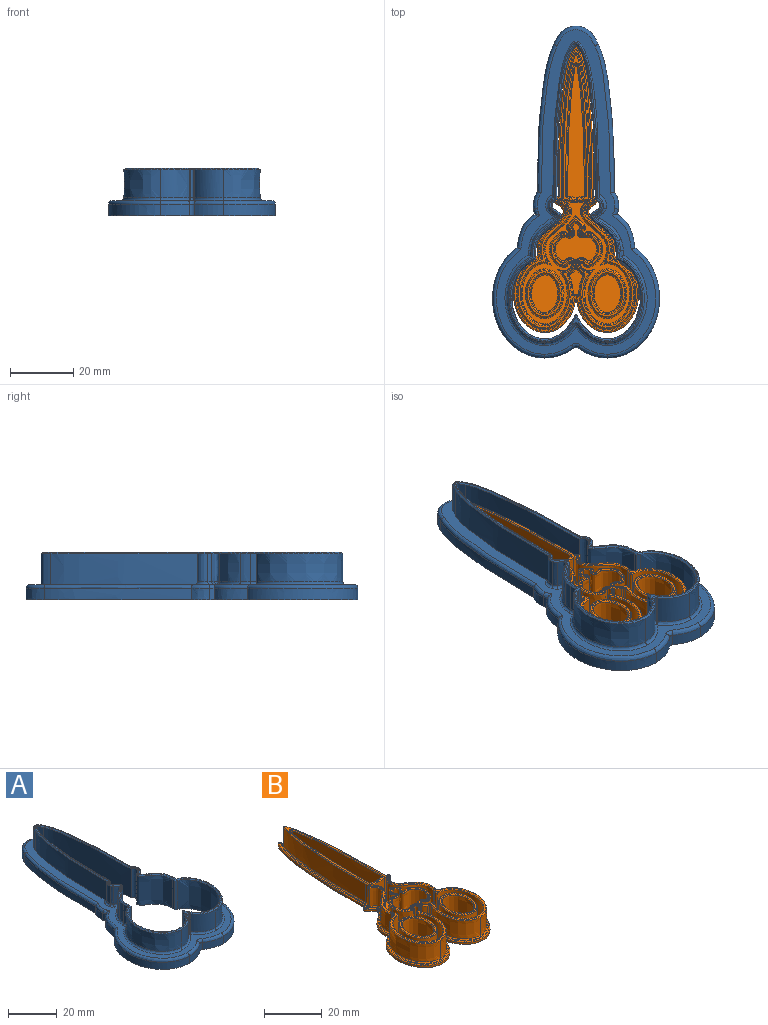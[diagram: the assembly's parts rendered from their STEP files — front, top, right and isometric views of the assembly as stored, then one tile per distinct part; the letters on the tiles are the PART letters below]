
ASSEMBLY  parts=2 mates=1
PART A: 138 faces, bbox 125.3x309.9x15.5 mm
  f0: extruded ~27.05x11.63mm, area 320.1mm2, adj f1,f15,f88,f136
  f1: extruded ~8.88x2.07mm, area 18.4mm2, adj f0,f2,f86,f137
  f2: extruded ~8.88x3.15mm, area 28.7mm2, adj f1,f3,f84,f135
  f3: extruded ~8.88x6.52mm, area 83.1mm2, adj f2,f16,f82,f133
  f4: extruded ~8.88x1.19mm, area 13.1mm2, adj f5,f16,f74,f129
  f5: extruded ~8.88x3.27mm, area 33.3mm2, adj f4,f6,f72,f127
  f6: extruded ~46.18x9.78mm, area 455.9mm2, adj f5,f7,f57,f72,f125
  f7: extruded ~9.78x5.38mm, area 83.8mm2, adj f6,f8,f57,f123
  f8: extruded ~46.22x9.78mm, area 456mm2, adj f7,f9,f57,f73,f121
  f9: extruded ~8.88x3.28mm, area 33.6mm2, adj f8,f10,f73,f119
  f10: extruded ~8.88x1.12mm, area 12.3mm2, adj f9,f17,f75,f117
  f11: extruded ~8.88x6.52mm, area 83.1mm2, adj f12,f17,f83,f114
  f12: extruded ~8.88x3.17mm, area 28.9mm2, adj f11,f18,f85,f116
  f13: extruded ~27.03x11.63mm, area 319.7mm2, adj f14,f18,f89,f120
  f14: extruded ~9.08x8.88mm, area 96.8mm2, adj f13,f19,f91,f122
  f15: extruded ~9.08x8.88mm, area 96.8mm2, adj f0,f22,f90,f134
  f16: extruded ~8.88x2.56mm, area 33mm2, adj f3,f4,f76,f78,f80,f131
  f17: extruded ~8.88x2.59mm, area 33.3mm2, adj f10,f11,f77,f79,f81,f115
  f18: extruded ~8.88x2.06mm, area 18.3mm2, adj f12,f13,f87,f118
  f19: extruded ~8.88x0.05mm, area 0.5mm2, adj f14,f20,f93,f124
  f20: extruded ~8.88x0.23mm, area 2.4mm2, adj f19,f95,f96,f126
  f21: extruded ~8.88x0.23mm, area 2.4mm2, adj f22,f94,f96,f130
  f22: extruded ~8.88x0.05mm, area 0.5mm2, adj f15,f21,f92,f132
  f23: extruded ~15.18x14.58mm, area 287.7mm2, adj f24,f40,f42,f102
  f24: extruded ~14.58x1.23mm, area 17.9mm2, adj f23,f25,f42,f103
  f25: extruded ~14.58x1.25mm, area 19.9mm2, adj f24,f26,f42,f104
  f26: extruded ~24.58x14.58mm, area 472.3mm2, adj f25,f27,f42,f105
  f27: extruded ~14.58x9.26mm, area 178mm2, adj f26,f28,f42,f106
  f28: extruded ~14.58x0.14mm, area 2.2mm2, adj f27,f29,f42,f106
  f29: extruded ~14.88x1.1mm, area 23.8mm2, adj f28,f30,f42,f106,f107
  f30: extruded ~14.58x0.14mm, area 2.2mm2, adj f29,f31,f42,f107
  f31: extruded ~14.58x9.26mm, area 178mm2, adj f30,f32,f42,f109
  f32: extruded ~24.58x14.58mm, area 472mm2, adj f31,f33,f42,f111
  f33: extruded ~14.58x1.25mm, area 19.7mm2, adj f32,f34,f42,f112
  f34: extruded ~14.58x1.22mm, area 17.9mm2, adj f33,f35,f42,f110
  f35: extruded ~15.1x14.58mm, area 286.2mm2, adj f34,f36,f42,f108
  f36: extruded ~14.76x2.94mm, area 45.4mm2, adj f35,f37,f42,f98,f108,f113
  f37: extruded ~46.33x14.58mm, area 681.9mm2, adj f36,f38,f42,f98
  f38: extruded ~14.58x3.23mm, area 86.1mm2, adj f37,f39,f42,f99
  f39: extruded ~46.32x14.58mm, area 682.2mm2, adj f38,f40,f42,f100
  f40: extruded ~14.58x2.36mm, area 43.4mm2, adj f23,f39,f42,f101
  f41: plane 94.61x42.81mm, normal (0,0,1), area 97.1mm2, adj f98,f99,f100,f101,f102,f103,f104,f105
  f42: plane 104.58x52.6mm, normal (0,0,-1), area 1523.6mm2, adj f23,f24,f25,f26,f27,f28,f29,f30
  f43: extruded ~10.54x5.63mm, area 44.7mm2, adj f42,f44,f56,f66
  f44: extruded ~34.78x16.43mm, area 166.3mm2, adj f42,f43,f45,f64
  f45: extruded ~9.14x3.6mm, area 35.4mm2, adj f42,f44,f46,f62
  f46: cylinder r=1.2mm len=3.6mm, axis (0,0,-1), area 5.6mm2, adj f42,f45,f47,f60
  f47: extruded ~9.14x3.6mm, area 35.4mm2, adj f42,f46,f48,f58
  f48: extruded ~34.78x16.43mm, area 166.3mm2, adj f42,f47,f49,f59
  f49: extruded ~10.53x5.63mm, area 44.7mm2, adj f42,f48,f50,f61
  f50: extruded ~3.6x1.55mm, area 5.9mm2, adj f42,f49,f51,f63,f65
  f51: extruded ~5.54x3.6mm, area 20.9mm2, adj f42,f50,f52,f65
  f52: extruded ~46.44x5.18mm, area 169.2mm2, adj f42,f51,f53,f67
  f53: extruded ~13.99x5.73mm, area 69.1mm2, adj f42,f52,f54,f69
  f54: extruded ~46.55x5.1mm, area 169.5mm2, adj f42,f53,f55,f71
  f55: extruded ~5.44x3.6mm, area 20.6mm2, adj f42,f54,f56,f70
  f56: extruded ~3.6x1.55mm, area 5.8mm2, adj f42,f43,f55,f68
  f57: plane 102.19x50.2mm, normal (0,0,1), area 781.1mm2, adj f6,f7,f8,f58,f59,f60,f61,f62
  f58: bspline ~11.07x5.19mm, area 18mm2, adj f47,f57,f59,f60
  f59: bspline ~35.48x27.64mm, area 85.5mm2, adj f48,f57,f58,f61
  f60: torus R=2.4mm, axis (0,0,-1), area 4mm2, adj f46,f57,f58,f62
  f61: bspline ~16.17x12.72mm, area 24.2mm2, adj f49,f57,f59,f63
  f62: bspline ~11.07x5.19mm, area 18mm2, adj f45,f57,f60,f64
  f63: bspline ~3.23x2.2mm, area 3.8mm2, adj f50,f57,f61,f65
  f64: bspline ~35.48x27.64mm, area 85.5mm2, adj f44,f57,f62,f66
  f65: bspline ~7.84x3.36mm, area 10.6mm2, adj f50,f51,f57,f63,f67
  f66: bspline ~17.19x13.49mm, area 24.2mm2, adj f43,f57,f64,f68
  f67: bspline ~64.82x9.6mm, area 88.6mm2, adj f52,f57,f65,f69
  f68: bspline ~3.55x2.44mm, area 3.8mm2, adj f56,f57,f66,f70
  f69: bspline ~20.23x12.76mm, area 34.5mm2, adj f53,f57,f67,f71
  f70: bspline ~6.73x2.7mm, area 10.6mm2, adj f55,f57,f68,f71
  f71: bspline ~261.75x110.62mm, area 88.8mm2, adj f54,f57,f69,f70
  f72: bspline ~4.93x3mm, area 6.3mm2, adj f5,f6,f57,f74
  f73: bspline ~5.31x3.48mm, area 6.4mm2, adj f8,f9,f57,f75
  f74: bspline ~2.52x2.18mm, area 2.4mm2, adj f4,f57,f72,f76
  f75: bspline ~2.24x2.03mm, area 2.2mm2, adj f10,f57,f73,f77
  f76: bspline ~2.36x1.96mm, area 2.2mm2, adj f16,f57,f74,f78
  f77: bspline ~2.38x1.96mm, area 2.3mm2, adj f17,f57,f75,f79
  f78: bspline ~1.09x1.03mm, area 0.7mm2, adj f16,f76,f80
  f79: bspline ~1.09x1.03mm, area 0.7mm2, adj f17,f77,f81
  f80: bspline ~1.39x1.32mm, area 0.9mm2, adj f16,f57,f78,f82
  f81: bspline ~1.41x1.32mm, area 0.9mm2, adj f17,f57,f79,f83
  f82: bspline ~11.13x10.28mm, area 13.5mm2, adj f3,f57,f80,f84
  f83: bspline ~11.04x10.19mm, area 13.5mm2, adj f11,f57,f81,f85
  f84: bspline ~4.22x1.67mm, area 4.7mm2, adj f2,f57,f82,f86
  f85: bspline ~4.66x1.85mm, area 4.7mm2, adj f12,f57,f83,f87
  f86: bspline ~3.08x0.98mm, area 2.6mm2, adj f1,f57,f84,f88
  f87: bspline ~3.17x1.01mm, area 2.6mm2, adj f18,f57,f85,f89
  f88: bspline ~28.88x24.5mm, area 51.8mm2, adj f0,f57,f86,f90
  f89: bspline ~28.88x24.5mm, area 51.7mm2, adj f13,f57,f87,f91
  f90: bspline ~10.44x6.32mm, area 15.9mm2, adj f15,f57,f88,f92
  f91: bspline ~10.44x6.32mm, area 15.9mm2, adj f14,f57,f89,f93
  f92: bspline ~0.9x0.79mm, area 0.1mm2, adj f22,f57,f90,f94
  f93: bspline ~0.9x0.79mm, area 0.1mm2, adj f19,f57,f91,f95
  f94: bspline ~1.75x1.59mm, area 0.3mm2, adj f21,f57,f92,f97
  f95: bspline ~1.17x1.12mm, area 0.3mm2, adj f20,f57,f93,f97
  f96: cylinder r=0.72mm len=8.88mm, axis (0,0,-1), area 12.9mm2, adj f20,f21,f97,f128
  f97: bspline ~1.68x1.22mm, area 1.4mm2, adj f94,f95,f96
  f98: bspline ~49.14x4.94mm, area 27.9mm2, adj f36,f37,f41,f99,f113
  f99: bspline ~3.98x2.81mm, area 3.8mm2, adj f38,f41,f98,f100
  f100: bspline ~48.87x5.02mm, area 27.8mm2, adj f39,f41,f99,f101
  f101: bspline ~3.13x1.97mm, area 1.9mm2, adj f40,f41,f100,f102
  f102: bspline ~15.36x8.68mm, area 11.7mm2, adj f23,f41,f101,f103
  f103: bspline ~1.28x0.53mm, area 0.6mm2, adj f24,f41,f102,f104
  f104: bspline ~1.51x0.95mm, area 0.7mm2, adj f25,f41,f103,f105
  f105: bspline ~25.38x10.85mm, area 19.6mm2, adj f26,f41,f104,f106
  f106: bspline ~10.25x8.72mm, area 7.8mm2, adj f27,f28,f29,f41,f105,f107
  f107: bspline ~0.96x0.72mm, area 0.4mm2, adj f29,f30,f41,f106,f109
  f108: bspline ~15.89x8.69mm, area 11.4mm2, adj f35,f36,f41,f110,f113
  f109: bspline ~9.64x7.28mm, area 7.4mm2, adj f31,f41,f107,f111
  f110: bspline ~1.35x0.55mm, area 0.6mm2, adj f34,f41,f108,f112
  f111: bspline ~25.37x10.9mm, area 19.6mm2, adj f32,f41,f109,f112
  f112: bspline ~1.44x0.93mm, area 0.7mm2, adj f33,f41,f110,f111
  f113: bspline ~7.94x2.39mm, area 1.2mm2, adj f36,f41,f98,f108
  f114: bspline ~6.78x6.62mm, area 5.5mm2, adj f11,f41,f115,f116
  f115: bspline ~3.23x2.22mm, area 2.4mm2, adj f17,f41,f114,f117
  f116: bspline ~3.21x1.07mm, area 1.9mm2, adj f12,f41,f114,f118
  f117: bspline ~1.27x1.05mm, area 0.8mm2, adj f10,f41,f115,f119
  f118: bspline ~2.35x0.48mm, area 1.3mm2, adj f18,f41,f116,f120
  f119: bspline ~3.68x1.98mm, area 2.2mm2, adj f9,f41,f117,f121
  f120: bspline ~27.9x11.7mm, area 21.1mm2, adj f13,f41,f118,f122
  f121: bspline ~48.77x5.01mm, area 27.8mm2, adj f8,f41,f119,f123
  f122: bspline ~9.08x5.43mm, area 6.3mm2, adj f14,f41,f120,f124
  f123: bspline ~5.38x3.24mm, area 4.8mm2, adj f7,f41,f121,f125
  f124: bspline ~0.43x0.4mm, area 0mm2, adj f19,f41,f122,f126
  f125: bspline ~48.74x5.1mm, area 27.7mm2, adj f6,f41,f123,f127
  f126: bspline ~0.51x0.46mm, area 0.2mm2, adj f20,f41,f124,f128
  f127: bspline ~3.41x1.79mm, area 2.1mm2, adj f5,f41,f125,f129
  f128: cone r=1.14mm half-angle=45deg, axis (0,0,1), area 1.1mm2, adj f41,f96,f126,f130
  f129: bspline ~1.4x1.13mm, area 0.8mm2, adj f4,f41,f127,f131
  f130: bspline ~0.5x0.46mm, area 0.2mm2, adj f21,f41,f128,f132
  f131: bspline ~3.22x2.19mm, area 2.4mm2, adj f16,f41,f129,f133
  f132: bspline ~0.42x0.39mm, area 0mm2, adj f22,f41,f130,f134
  f133: bspline ~6.78x6.62mm, area 5.5mm2, adj f3,f41,f131,f135
  f134: bspline ~9.08x5.44mm, area 6.4mm2, adj f15,f41,f132,f136
  f135: bspline ~3.18x1.07mm, area 1.9mm2, adj f2,f41,f133,f137
  f136: bspline ~27.91x11.7mm, area 21.2mm2, adj f0,f41,f134,f137
  f137: bspline ~2.47x0.51mm, area 1.3mm2, adj f1,f41,f135,f136
PART B: 271 faces, bbox 39.8x91x10 mm
  f0: bspline ~0.98x0.72mm, area 0.4mm2, adj f35,f36,f124,f126,f193,f194
  f1: bspline ~0.98x0.72mm, area 0.4mm2, adj f63,f64,f131,f133,f189,f190
  f2: bspline ~0.96x0.77mm, area 0.4mm2, adj f64,f65,f129,f131,f187,f188
  f3: bspline ~0.99x0.38mm, area 0.4mm2, adj f55,f56,f93,f97,f184,f186
  f4: bspline ~0.97x0.44mm, area 0.4mm2, adj f49,f50,f92,f96,f181,f182
  f5: bspline ~0.96x0.77mm, area 0.4mm2, adj f34,f35,f122,f124,f179,f180
  f6: bspline ~1.13x0.57mm, area 0.6mm2, adj f52,f53,f88,f89,f177,f178
  f7: plane 41.66x5.5mm, normal (0,0,1), area 170.5mm2, adj f145,f146,f147,f174
  f8: plane 13.16x11.87mm, normal (0,0,1), area 87.1mm2, adj f112,f113,f114,f166
  f9: plane 89.88x38.68mm, normal (0,0,1), area 128.8mm2, adj f88,f89,f90,f91,f92,f93,f94,f95
  f10: plane 38.56x33.88mm, normal (0,0,1), area 188.9mm2, adj f116,f117,f118,f119,f120,f121,f122,f123
  f11: plane 0.84x0.09mm, normal (0,-1,0), area 0.1mm2, adj f12,f25,f26,f158
  f12: extruded ~11.61x9.82mm, area 14.1mm2, adj f11,f13,f26,f160
  f13: extruded ~24.09x9.83mm, area 27.4mm2, adj f12,f14,f26,f162
  f14: extruded ~17.1x8.23mm, area 18.2mm2, adj f13,f15,f26,f161
  f15: extruded ~0.84x0.72mm, area 0.6mm2, adj f14,f16,f26,f159
  f16: extruded ~1.18x1.08mm, area 1.4mm2, adj f15,f17,f26,f157
  f17: extruded ~46.34x4.42mm, area 39.3mm2, adj f16,f18,f26,f155
  f18: plane 0.96x0.84mm, normal (0.87,0.5,0), area 0.9mm2, adj f17,f26,f153,f175
  f19: plane 0.97x0.84mm, normal (-0.87,0.5,0), area 0.9mm2, adj f20,f26,f151,f175
  f20: extruded ~46.38x4.5mm, area 39.3mm2, adj f19,f21,f26,f149
  f21: extruded ~1.23x1.15mm, area 1.4mm2, adj f20,f22,f26,f148
  f22: extruded ~0.84x0.61mm, area 0.5mm2, adj f21,f23,f26,f150
  f23: extruded ~17.1x8.18mm, area 18.2mm2, adj f22,f24,f26,f152
  f24: extruded ~24.09x9.83mm, area 27.4mm2, adj f23,f25,f26,f154
  f25: extruded ~11.61x9.82mm, area 14.1mm2, adj f11,f24,f26,f156
  f26: plane 90.6x39.4mm, normal (0,0,-1), area 1541.7mm2, adj f11,f12,f13,f14,f15,f16,f17,f18
  f27: extruded ~41.23x7.74mm, area 320.1mm2, adj f28,f147,f173,f269
  f28: extruded ~7.74x6.14mm, area 49.1mm2, adj f27,f70,f145,f267
  f29: extruded ~7.74x6.04mm, area 47.5mm2, adj f30,f69,f119,f229
  f30: extruded ~7.74x0.89mm, area 7.2mm2, adj f29,f117,f195,f231
  f31: extruded ~7.74x0.9mm, area 7.9mm2, adj f32,f116,f195,f234
  f32: extruded ~16.14x8.27mm, area 152.3mm2, adj f31,f33,f118,f232
  f33: extruded ~7.74x1.22mm, area 10mm2, adj f32,f34,f120,f230
  f34: extruded ~7.74x0.32mm, area 2.7mm2, adj f5,f33,f122,f179,f228
  f35: extruded ~19.56x14.85mm, area 365.8mm2, adj f0,f5,f124,f179,f193,f224
  f36: extruded ~7.74x0.35mm, area 2.7mm2, adj f0,f37,f126,f193,f220
  f37: extruded ~7.74x1.12mm, area 9.5mm2, adj f36,f38,f128,f218
  f38: extruded ~7.74x2.23mm, area 21mm2, adj f37,f39,f130,f216
  f39: extruded ~7.74x6.69mm, area 82.2mm2, adj f38,f40,f132,f214
  f40: extruded ~7.74x6.37mm, area 71.6mm2, adj f39,f41,f134,f212
  f41: extruded ~7.74x4.59mm, area 45.4mm2, adj f40,f136,f191,f210
  f42: extruded ~12.81x7.74mm, area 184.3mm2, adj f86,f114,f165,f235
  f43: extruded ~7.74x2.02mm, area 20.1mm2, adj f44,f87,f108,f249
  f44: extruded ~7.74x0.52mm, area 4.7mm2, adj f43,f106,f163,f247
  f45: extruded ~16.55x8.63mm, area 164mm2, adj f46,f104,f163,f243
  f46: extruded ~21.74x8.63mm, area 225.6mm2, adj f45,f47,f102,f241
  f47: extruded ~7.74x0.39mm, area 3.1mm2, adj f46,f100,f171,f239
  f48: extruded ~7.74x0.55mm, area 4.3mm2, adj f49,f98,f171,f242
  f49: extruded ~16.42x8.3mm, area 160.7mm2, adj f4,f48,f96,f181,f244
  f50: extruded ~7.74x0.98mm, area 8.8mm2, adj f4,f51,f92,f181,f248
  f51: extruded ~7.74x1.28mm, area 9.9mm2, adj f50,f52,f90,f250
  f52: extruded ~43.93x7.74mm, area 342.3mm2, adj f6,f51,f88,f177,f252
  f53: extruded ~43.97x7.74mm, area 342.8mm2, adj f6,f54,f89,f177,f256
  f54: extruded ~7.74x1.28mm, area 9.9mm2, adj f53,f55,f91,f258
  f55: extruded ~7.74x0.93mm, area 8.2mm2, adj f3,f54,f93,f184,f260
  f56: extruded ~16.42x8.33mm, area 160.6mm2, adj f3,f57,f97,f184,f264
  f57: extruded ~7.74x0.51mm, area 4.1mm2, adj f56,f99,f169,f266
  f58: extruded ~7.74x0.48mm, area 3.9mm2, adj f59,f101,f169,f263
  f59: extruded ~21.72x8.63mm, area 225mm2, adj f58,f60,f103,f261
  f60: extruded ~16.56x8.63mm, area 164.1mm2, adj f59,f105,f167,f259
  f61: extruded ~7.74x0.49mm, area 4.4mm2, adj f81,f107,f167,f255
  f62: extruded ~7.74x1.12mm, area 9.5mm2, adj f63,f80,f135,f207
  f63: extruded ~7.74x0.35mm, area 2.7mm2, adj f1,f62,f133,f189,f209
  f64: extruded ~19.56x14.85mm, area 365.8mm2, adj f1,f2,f131,f187,f189,f213
  f65: extruded ~7.74x0.32mm, area 2.7mm2, adj f2,f66,f129,f187,f217
  f66: extruded ~7.74x1.22mm, area 10mm2, adj f65,f67,f127,f219
  f67: extruded ~16.14x8.27mm, area 152.3mm2, adj f66,f68,f125,f221
  f68: extruded ~7.74x0.99mm, area 8.7mm2, adj f67,f123,f197,f223
  f69: extruded ~7.74x0.99mm, area 7.9mm2, adj f29,f121,f197,f227
  f70: extruded ~41.23x7.74mm, area 320.1mm2, adj f28,f146,f173,f268
  f71: plane 86.49x36.98mm, normal (0,0,1), area 169.2mm2, adj f203,f204,f205,f206,f207,f208,f209,f210
  f72: extruded ~12.59x9.07mm, area 264.4mm2, adj f144,f201
  f73: extruded ~14.99x11.47mm, area 323.2mm2, adj f143,f202
  f74: plane 14.46x10.94mm, normal (0,0,1), area 22.7mm2, adj f201,f202
  f75: plane 11.88x8.35mm, normal (0,0,1), area 77.6mm2, adj f144
  f76: extruded ~12.59x9.07mm, area 264.4mm2, adj f142,f199
  f77: extruded ~14.99x11.47mm, area 323.2mm2, adj f141,f200
  f78: plane 14.46x10.94mm, normal (0,0,1), area 22.7mm2, adj f199,f200
  f79: plane 11.88x8.35mm, normal (0,0,1), area 77.6mm2, adj f142
  f80: extruded ~7.74x2.3mm, area 22.1mm2, adj f62,f85,f137,f205
  f81: extruded ~7.74x2.03mm, area 20.1mm2, adj f61,f87,f109,f253
  f82: extruded ~12.79x7.74mm, area 183.2mm2, adj f86,f111,f112,f113,f165,f238
  f83: extruded ~7.74x4.61mm, area 45.6mm2, adj f84,f138,f191,f206
  f84: extruded ~7.74x6.35mm, area 70.9mm2, adj f83,f85,f140,f204
  f85: extruded ~7.74x6.57mm, area 81.6mm2, adj f80,f84,f139,f203
  f86: cylinder r=0.06mm len=7.74mm, axis (0,0,-1), area 1.2mm2, adj f42,f82,f115,f236
  f87: cylinder r=0.06mm len=7.74mm, axis (0,0,-1), area 1.2mm2, adj f43,f81,f110,f251
  f88: bspline ~58.05x5.22mm, area 25.4mm2, adj f6,f9,f52,f90,f178
  f89: bspline ~58.03x5.28mm, area 25.4mm2, adj f6,f9,f53,f91,f178
  f90: bspline ~1.79x0.4mm, area 0.7mm2, adj f9,f51,f88,f92
  f91: bspline ~3.26x0.46mm, area 0.7mm2, adj f9,f54,f89,f93
  f92: bspline ~2x1.48mm, area 0.7mm2, adj f4,f9,f50,f90,f94,f182
  f93: bspline ~2.05x1.46mm, area 0.7mm2, adj f3,f9,f55,f91,f95,f186
  f94: bspline ~1.29x1.16mm, area 0.1mm2, adj f9,f92,f183
  f95: bspline ~0.94x0.81mm, area 0.1mm2, adj f9,f93,f185
  f96: bspline ~21.43x8.67mm, area 11.8mm2, adj f4,f9,f49,f98,f182,f183
  f97: bspline ~25.15x8.7mm, area 11.8mm2, adj f3,f9,f56,f99,f185,f186
  f98: bspline ~1.13x0.57mm, area 0.3mm2, adj f9,f48,f96,f172
  f99: bspline ~0.98x0.57mm, area 0.3mm2, adj f9,f57,f97,f170
  f100: bspline ~0.87x0.54mm, area 0.2mm2, adj f9,f47,f102,f172
  f101: bspline ~0.97x0.57mm, area 0.3mm2, adj f9,f58,f103,f170
  f102: bspline ~24.68x17.66mm, area 16.7mm2, adj f9,f46,f100,f104
  f103: bspline ~23x17.65mm, area 16.6mm2, adj f9,f59,f101,f105
  f104: bspline ~17.36x10.35mm, area 12.1mm2, adj f9,f45,f102,f164
  f105: bspline ~17.95x14.41mm, area 12.1mm2, adj f9,f60,f103,f168
  f106: bspline ~1.2x0.95mm, area 0.4mm2, adj f9,f44,f108,f164
  f107: bspline ~1.12x0.88mm, area 0.3mm2, adj f9,f61,f109,f168
  f108: bspline ~2.92x2.64mm, area 1.3mm2, adj f9,f43,f106,f110
  f109: bspline ~2.89x2.63mm, area 1.3mm2, adj f9,f81,f107,f110
  f110: bspline ~1.02x0.42mm, area 0.1mm2, adj f87,f108,f109
  f111: bspline ~0.36x0.36mm, area 0.1mm2, adj f82,f112,f113
  f112: bspline ~1.93x1.75mm, area 1.1mm2, adj f8,f82,f111,f166
  f113: bspline ~11.36x7.26mm, area 12mm2, adj f8,f82,f111,f115
  f114: bspline ~13.05x7.28mm, area 13.1mm2, adj f8,f42,f115,f166
  f115: bspline ~1.02x0.42mm, area 0.1mm2, adj f86,f113,f114
  f116: bspline ~1.54x1.03mm, area 0.5mm2, adj f10,f31,f118,f196
  f117: bspline ~1.41x0.73mm, area 0.4mm2, adj f10,f30,f119,f196
  f118: bspline ~17.76x8.64mm, area 11.2mm2, adj f10,f32,f116,f120
  f119: bspline ~6.77x0.94mm, area 3.5mm2, adj f10,f29,f117,f121
  f120: bspline ~3.11x1.18mm, area 0.7mm2, adj f10,f33,f118,f122
  f121: bspline ~1.46x0.67mm, area 0.4mm2, adj f10,f69,f119,f198
  f122: bspline ~3.26x2.28mm, area 0.7mm2, adj f5,f10,f34,f120,f180
  f123: bspline ~1.77x1.22mm, area 0.6mm2, adj f10,f68,f125,f198
  f124: bspline ~19.56x14.86mm, area 27.1mm2, adj f0,f5,f10,f35,f180,f194
  f125: bspline ~19.76x8.64mm, area 11.2mm2, adj f10,f67,f123,f127
  f126: bspline ~5.33x0.83mm, area 0.6mm2, adj f0,f10,f36,f128,f194
  f127: bspline ~3.18x1.5mm, area 0.7mm2, adj f10,f66,f125,f129
  f128: bspline ~1.61x0.95mm, area 0.7mm2, adj f10,f37,f126,f130
  f129: bspline ~3.26x2.28mm, area 0.7mm2, adj f2,f10,f65,f127,f188
  f130: bspline ~2.55x1.41mm, area 1.4mm2, adj f10,f38,f128,f132
  f131: bspline ~19.56x14.86mm, area 27.2mm2, adj f1,f2,f10,f64,f188,f190
  f132: bspline ~8.91x7.16mm, area 6.1mm2, adj f10,f39,f130,f134
  f133: bspline ~3.39x0.79mm, area 0.6mm2, adj f1,f10,f63,f135,f190
  f134: bspline ~8.31x7.36mm, area 5.2mm2, adj f10,f40,f132,f136
  f135: bspline ~3.23x1.25mm, area 0.7mm2, adj f10,f62,f133,f137
  f136: bspline ~6.39x3.58mm, area 3.6mm2, adj f10,f41,f134,f192
  f137: bspline ~2.74x1.41mm, area 1.5mm2, adj f10,f80,f135,f139
  f138: bspline ~11.2x8.69mm, area 3.6mm2, adj f10,f83,f140,f192
  f139: bspline ~8.91x8.5mm, area 6mm2, adj f10,f85,f137,f140
  f140: bspline ~7.51x6.89mm, area 5.4mm2, adj f10,f84,f138,f139
  f141: bspline ~15.72x12.2mm, area 24.1mm2, adj f10,f77
  f142: bspline ~12.6x9.07mm, area 18.9mm2, adj f76,f79
  f143: bspline ~15.72x12.2mm, area 24.1mm2, adj f10,f73
  f144: bspline ~12.6x9.07mm, area 18.9mm2, adj f72,f75
  f145: bspline ~6.37x1.07mm, area 3.4mm2, adj f7,f28,f146,f147
  f146: bspline ~42.81x3.1mm, area 23.3mm2, adj f7,f70,f145,f174
  f147: bspline ~45.13x3.15mm, area 23.3mm2, adj f7,f27,f145,f174
  f148: bspline ~1.71x1.54mm, area 1mm2, adj f9,f21,f149,f150
  f149: bspline ~48.53x5.02mm, area 26.5mm2, adj f9,f20,f148,f151
  f150: bspline ~0.73x0.51mm, area 0.3mm2, adj f9,f22,f148,f152
  f151: cylinder r=0.36mm len=1.15mm, axis (0.5,0.87,0), area 0.6mm2, adj f9,f19,f149,f176
  f152: bspline ~18.49x8.56mm, area 12.3mm2, adj f9,f23,f150,f154
  f153: cylinder r=0.36mm len=1.14mm, axis (0.5,-0.87,0), area 0.6mm2, adj f9,f18,f155,f176
  f154: bspline ~24.2x20.1mm, area 18.3mm2, adj f9,f24,f152,f156
  f155: bspline ~47.92x4.86mm, area 26.5mm2, adj f9,f17,f153,f157
  f156: bspline ~13.05x12.22mm, area 9.5mm2, adj f9,f25,f154,f158
  f157: bspline ~1.97x1.83mm, area 0.9mm2, adj f9,f16,f155,f159
  f158: cylinder r=0.36mm len=0.78mm, axis (-1,0,0), area 0.2mm2, adj f9,f11,f156,f160
  f159: bspline ~0.88x0.61mm, area 0.4mm2, adj f9,f15,f157,f161
  f160: bspline ~12.22x10.66mm, area 9.5mm2, adj f9,f12,f158,f162
  f161: bspline ~18.52x8.6mm, area 12.3mm2, adj f9,f14,f159,f162
  f162: bspline ~24.2x20.1mm, area 18.3mm2, adj f9,f13,f160,f161
  f163: cylinder r=0.6mm len=7.74mm, axis (0,0,-1), area 7.1mm2, adj f44,f45,f164,f245
  f164: torus R=0.24mm, axis (0,0,1), area 0.4mm2, adj f9,f104,f106,f163
  f165: cylinder r=0.6mm len=7.74mm, axis (0,0,-1), area 6.6mm2, adj f42,f82,f166,f237
  f166: torus R=0.24mm, axis (0,0,1), area 0.4mm2, adj f8,f112,f114,f165
  f167: cylinder r=0.6mm len=7.74mm, axis (0,0,-1), area 7.5mm2, adj f60,f61,f168,f257
  f168: torus R=0.24mm, axis (0,0,1), area 0.4mm2, adj f9,f105,f107,f167
  f169: cylinder r=0.6mm len=7.74mm, axis (0,0,-1), area 7.7mm2, adj f57,f58,f170,f265
  f170: torus R=0.24mm, axis (0,0,1), area 0.4mm2, adj f9,f99,f101,f169
  f171: cylinder r=0.6mm len=7.74mm, axis (0,0,-1), area 7.4mm2, adj f47,f48,f172,f240
  f172: torus R=0.24mm, axis (0,0,1), area 0.4mm2, adj f9,f98,f100,f171
  f173: cylinder r=0.6mm len=7.74mm, axis (0,0,-1), area 12.6mm2, adj f27,f70,f174,f270
  f174: torus R=0.24mm, axis (0,0,1), area 0.7mm2, adj f7,f146,f147,f173
  f175: cylinder r=0.6mm len=1.04mm, axis (0,0,1), area 1.1mm2, adj f18,f19,f26,f176
  f176: torus R=0.24mm, axis (0,0,1), area 0.6mm2, adj f9,f151,f153,f175
  f177: cylinder r=0.6mm len=7.48mm, axis (0,0,-1), area 10.9mm2, adj f6,f52,f53,f254
  f178: bspline ~1.88x1.01mm, area 0.5mm2, adj f6,f88,f89
  f179: cylinder r=0.6mm len=7.61mm, axis (0,0,-1), area 9.4mm2, adj f5,f34,f35,f226
  f180: bspline ~1.97x1.58mm, area 0.5mm2, adj f5,f122,f124
  f181: cylinder r=0.6mm len=7.42mm, axis (0,0,-1), area 8.4mm2, adj f4,f49,f50,f246
  f182: bspline ~0.94x0.6mm, area 0.1mm2, adj f4,f92,f96,f183
  f183: bspline ~0.76x0.73mm, area 0.2mm2, adj f94,f96,f182
  f184: cylinder r=0.6mm len=7.48mm, axis (0,0,-1), area 8.7mm2, adj f3,f55,f56,f262
  f185: bspline ~0.76x0.72mm, area 0.2mm2, adj f95,f97,f186
  f186: bspline ~0.96x0.6mm, area 0.2mm2, adj f3,f93,f97,f185
  f187: cylinder r=0.6mm len=7.61mm, axis (0,0,-1), area 9.4mm2, adj f2,f64,f65,f215
  f188: bspline ~1.97x1.58mm, area 0.5mm2, adj f2,f129,f131
  f189: cylinder r=0.6mm len=7.6mm, axis (0,0,-1), area 9.3mm2, adj f1,f63,f64,f211
  f190: bspline ~2.04x1.47mm, area 0.5mm2, adj f1,f131,f133
  f191: cylinder r=0.6mm len=7.74mm, axis (0,0,-1), area 7.4mm2, adj f41,f83,f192,f208
  f192: bspline ~0.96x0.86mm, area 0.2mm2, adj f136,f138,f191
  f193: cylinder r=0.6mm len=7.6mm, axis (0,0,-1), area 9.3mm2, adj f0,f35,f36,f222
  f194: bspline ~2.04x1.47mm, area 0.5mm2, adj f0,f124,f126
  f195: cylinder r=0.24mm len=7.74mm, axis (0,0,-1), area 4.5mm2, adj f30,f31,f196,f233
  f196: bspline ~0.59x0.45mm, area 0.3mm2, adj f116,f117,f195
  f197: cylinder r=0.24mm len=7.74mm, axis (0,0,-1), area 4.5mm2, adj f68,f69,f198,f225
  f198: bspline ~1.06x0.5mm, area 0.3mm2, adj f121,f123,f197
  f199: bspline ~13.19x9.67mm, area 14.9mm2, adj f76,f78
  f200: bspline ~15x11.47mm, area 17.3mm2, adj f77,f78
  f201: bspline ~13.19x9.67mm, area 14.9mm2, adj f72,f74
  f202: bspline ~15x11.47mm, area 17.3mm2, adj f73,f74
  f203: bspline ~6.75x5.66mm, area 4.4mm2, adj f71,f85,f204,f205
  f204: bspline ~6.62x4.92mm, area 3.9mm2, adj f71,f84,f203,f206
  f205: bspline ~2.82x1.39mm, area 1.3mm2, adj f71,f80,f203,f207
  f206: bspline ~4.75x2.53mm, area 2.5mm2, adj f71,f83,f204,f208
  f207: bspline ~1.29x0.77mm, area 0.5mm2, adj f62,f71,f205,f209
  f208: cone r=0.3mm half-angle=45deg, axis (0,0,-1), area 0.3mm2, adj f71,f191,f206,f210
  f209: bspline ~0.4x0.34mm, area 0.2mm2, adj f63,f71,f207,f211
  f210: bspline ~4.71x2.52mm, area 2.5mm2, adj f41,f71,f208,f212
  f211: cone r=0.3mm half-angle=45deg, axis (0,0,-1), area 0.4mm2, adj f71,f189,f209,f213
  f212: bspline ~6.64x4.97mm, area 3.9mm2, adj f40,f71,f210,f214
  f213: bspline ~20.28x15.53mm, area 20.4mm2, adj f64,f71,f211,f215
  f214: bspline ~6.91x5.6mm, area 4.4mm2, adj f39,f71,f212,f216
  f215: cone r=0.3mm half-angle=45deg, axis (0,0,-1), area 0.4mm2, adj f71,f187,f213,f217
  f216: bspline ~2.71x1.38mm, area 1.3mm2, adj f38,f71,f214,f218
  f217: bspline ~0.45x0.42mm, area 0.2mm2, adj f65,f71,f215,f219
  f218: bspline ~1.29x0.77mm, area 0.5mm2, adj f37,f71,f216,f220
  f219: bspline ~1.34x0.7mm, area 0.6mm2, adj f66,f71,f217,f221
  f220: bspline ~0.4x0.34mm, area 0.2mm2, adj f36,f71,f218,f222
  f221: bspline ~16.22x8.56mm, area 8.3mm2, adj f67,f71,f219,f223
  f222: cone r=0.3mm half-angle=45deg, axis (0,0,-1), area 0.4mm2, adj f71,f193,f220,f224
  f223: bspline ~1.15x0.77mm, area 0.5mm2, adj f68,f71,f221,f225
  f224: bspline ~20.28x15.53mm, area 20.4mm2, adj f35,f71,f222,f226
  f225: cone r=0.54mm half-angle=45deg, axis (0,0,1), area 0.4mm2, adj f71,f197,f223,f227
  f226: cone r=0.3mm half-angle=45deg, axis (0,0,-1), area 0.4mm2, adj f71,f179,f224,f228
  f227: bspline ~1.23x0.55mm, area 0.5mm2, adj f69,f71,f225,f229
  f228: bspline ~0.45x0.42mm, area 0.2mm2, adj f34,f71,f226,f230
  f229: bspline ~6.77x0.89mm, area 2.6mm2, adj f29,f71,f227,f231
  f230: bspline ~1.34x0.7mm, area 0.6mm2, adj f33,f71,f228,f232
  f231: bspline ~1.09x0.58mm, area 0.4mm2, adj f30,f71,f229,f233
  f232: bspline ~16.21x8.56mm, area 8.3mm2, adj f32,f71,f230,f234
  f233: cone r=0.54mm half-angle=45deg, axis (0,0,1), area 0.4mm2, adj f71,f195,f231,f234
  f234: bspline ~1.02x0.7mm, area 0.4mm2, adj f31,f71,f232,f233
  f235: bspline ~13.11x7.19mm, area 10.2mm2, adj f42,f71,f236,f237
  f236: cone r=0.36mm half-angle=45deg, axis (0,0,1), area 0.2mm2, adj f71,f86,f235,f238
  f237: cone r=0.9mm half-angle=45deg, axis (0,0,1), area 0.4mm2, adj f71,f165,f235,f238
  f238: bspline ~13.08x7.18mm, area 10.2mm2, adj f71,f82,f236,f237
  f239: bspline ~0.45x0.38mm, area 0.2mm2, adj f47,f71,f240,f241
  f240: cone r=0.9mm half-angle=45deg, axis (0,0,1), area 0.5mm2, adj f71,f171,f239,f242
  f241: bspline ~21.74x8.68mm, area 12.2mm2, adj f46,f71,f239,f243
  f242: bspline ~0.6x0.41mm, area 0.2mm2, adj f48,f71,f240,f244
  f243: bspline ~16.55x8.68mm, area 8.9mm2, adj f45,f71,f241,f245
  f244: bspline ~16.68x8.66mm, area 8.9mm2, adj f49,f71,f242,f246
  f245: cone r=0.9mm half-angle=45deg, axis (0,0,1), area 0.5mm2, adj f71,f163,f243,f247
  f246: cone r=0.3mm half-angle=45deg, axis (0,0,-1), area 0.4mm2, adj f71,f181,f244,f248
  f247: bspline ~0.65x0.57mm, area 0.2mm2, adj f44,f71,f245,f249
  f248: bspline ~1.29x0.88mm, area 0.5mm2, adj f50,f71,f246,f250
  f249: bspline ~2.09x1.74mm, area 1.1mm2, adj f43,f71,f247,f251
  f250: bspline ~1.56x0.33mm, area 0.6mm2, adj f51,f71,f248,f252
  f251: cone r=0.36mm half-angle=45deg, axis (0,0,1), area 0.2mm2, adj f71,f87,f249,f253
  f252: bspline ~43.93x4.04mm, area 18.7mm2, adj f52,f71,f250,f254
  f253: bspline ~2.1x1.73mm, area 1.1mm2, adj f71,f81,f251,f255
  f254: cone r=0.3mm half-angle=45deg, axis (0,0,-1), area 0.5mm2, adj f71,f177,f252,f256
  f255: bspline ~0.6x0.52mm, area 0.2mm2, adj f61,f71,f253,f257
  f256: bspline ~43.97x4.12mm, area 18.8mm2, adj f53,f71,f254,f258
  f257: cone r=0.9mm half-angle=45deg, axis (0,0,1), area 0.5mm2, adj f71,f167,f255,f259
  f258: bspline ~1.49x0.35mm, area 0.6mm2, adj f54,f71,f256,f260
  f259: bspline ~16.56x8.65mm, area 8.9mm2, adj f60,f71,f257,f261
  f260: bspline ~1.29x0.86mm, area 0.5mm2, adj f55,f71,f258,f262
  f261: bspline ~21.72x8.68mm, area 12.1mm2, adj f59,f71,f259,f263
  f262: cone r=0.3mm half-angle=45deg, axis (0,0,-1), area 0.4mm2, adj f71,f184,f260,f264
  f263: bspline ~0.54x0.41mm, area 0.2mm2, adj f58,f71,f261,f265
  f264: bspline ~16.68x8.69mm, area 8.9mm2, adj f56,f71,f262,f266
  f265: cone r=0.9mm half-angle=45deg, axis (0,0,1), area 0.5mm2, adj f71,f169,f263,f266
  f266: bspline ~0.58x0.42mm, area 0.2mm2, adj f57,f71,f264,f265
  f267: bspline ~7.34x1.23mm, area 2.8mm2, adj f28,f71,f268,f269
  f268: bspline ~43.56x2.82mm, area 17.6mm2, adj f70,f71,f267,f270
  f269: bspline ~43.55x2.82mm, area 17.6mm2, adj f27,f71,f267,f270
  f270: cone r=0.9mm half-angle=45deg, axis (0,0,1), area 0.9mm2, adj f71,f173,f268,f269
PLACE A t=(-12.2,-10.02,0.52)mm
PLACE B t=(-12.21,-8.57,0.52)mm
MATE fastened A.f42 <-> B.f26  axis (0,0,-1) through (-12.22,-11.59,0.52)mm
